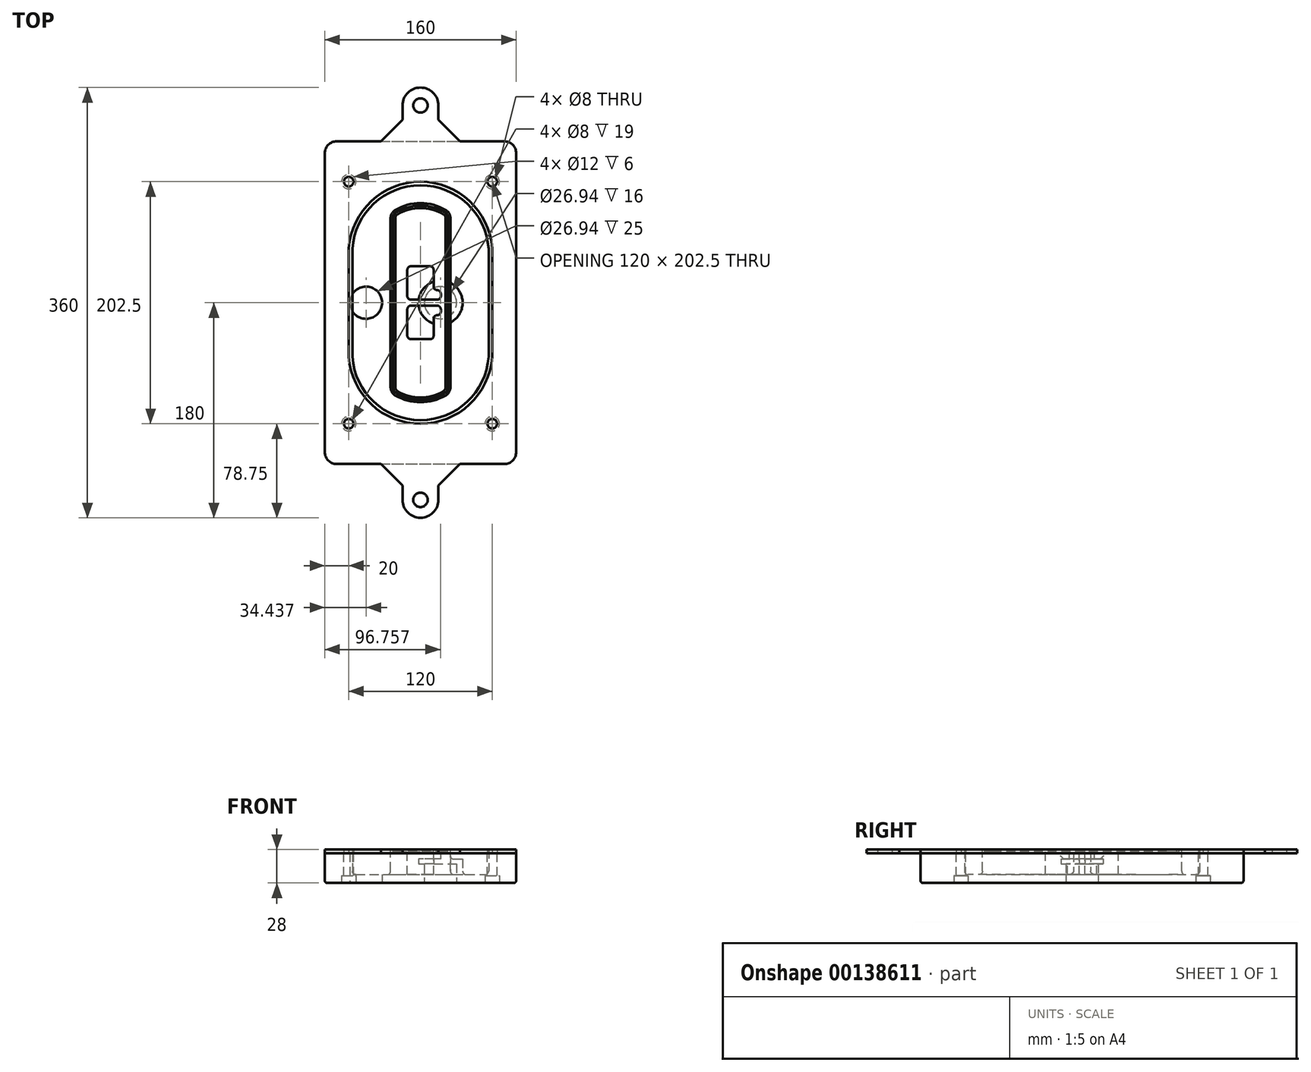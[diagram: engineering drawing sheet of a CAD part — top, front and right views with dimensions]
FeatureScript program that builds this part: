
annotation { "Feature Type Name" : "Feature", "Feature Type Description" : "" }
export const myFeature = defineFeature(function(context is Context, id is Id, definition is map)
    precondition{}
    {
        {
            var Q0;
            Q0=qCreatedBy(makeId("Top.planeOp"),FACE);
            var sketch = newSketch(context, id + "F0", { "sketchPlane" : qUnion([Q0])});
            skPoint(sketch, "E0.rect.middle", {"position": v(0, 0) * mm});
            skLineSegment(sketch, "E1.bottom", {"start": v(-70, -135) * mm, "end": v(70, -135) * mm});
            skLineSegment(sketch, "E1.top", {"start": v(-70, 135) * mm, "end": v(70, 135) * mm});
            skLineSegment(sketch, "E1.left", {"start": v(-80, -125) * mm, "end": v(-80, 125) * mm});
            skLineSegment(sketch, "E1.right", {"start": v(80, -125) * mm, "end": v(80, 125) * mm});
            skLineSegment(sketch, "E2", {"start": v(-80, 135) * mm, "end": v(80, -135) * mm, "construction": true});
            skLineSegment(sketch, "E3", {"start": v(80, 135) * mm, "end": v(-80, -135) * mm, "construction": true});
            skCircle(sketch, "E4", {"center": v(-60, 101.25) * mm, "radius": 4 * mm});
            skCircle(sketch, "E5", {"center": v(60, 101.25) * mm, "radius": 4 * mm});
            skCircle(sketch, "E6", {"center": v(60, -101.25) * mm, "radius": 4 * mm});
            skCircle(sketch, "E7", {"center": v(-60, -101.25) * mm, "radius": 4 * mm});
            skLineSegment(sketch, "E8", {"start": v(-60, 101.25) * mm, "end": v(60, 101.25) * mm, "construction": true});
            skLineSegment(sketch, "E9", {"start": v(60, 101.25) * mm, "end": v(60, -101.25) * mm, "construction": true});
            skLineSegment(sketch, "E10", {"start": v(60, -101.25) * mm, "end": v(-60, -101.25) * mm, "construction": true});
            skLineSegment(sketch, "E11", {"start": v(-60, -101.25) * mm, "end": v(-60, 101.25) * mm, "construction": true});
            skLineSegment(sketch, "E12", {"start": v(-60, 44.66) * mm, "end": v(-60, -44.66) * mm});
            skLineSegment(sketch, "E13", {"start": v(60, 44.66) * mm, "end": v(60, -44.66) * mm});
            skArc(sketch, "E14", {"start": v(59.98, 45.37) * mm, "mid": v(0, 101.25) * mm, "end": v(-59.98, 45.37) * mm});
            skArc(sketch, "E15", {"start": v(-59.98, -45.37) * mm, "mid": v(0, -101.25) * mm, "end": v(59.98, -45.37) * mm});
            skLineSegment(sketch, "E16", {"start": v(-60, 0) * mm, "end": v(60, 0) * mm, "construction": true});
            skPoint(sketch, "E17.visualSharp", {"position": v(-60, -45) * mm});
            skArc(sketch, "E17.filletArc", {"start": v(-60, -44.66) * mm, "mid": v(-60, -45.02) * mm, "end": v(-59.98, -45.37) * mm});
            skPoint(sketch, "E18.visualSharp", {"position": v(-60, 45) * mm});
            skArc(sketch, "E18.filletArc", {"start": v(-59.98, 45.37) * mm, "mid": v(-60, 45.02) * mm, "end": v(-60, 44.66) * mm});
            skPoint(sketch, "E19.visualSharp", {"position": v(60, 45) * mm});
            skArc(sketch, "E19.filletArc", {"start": v(60, 44.66) * mm, "mid": v(60, 45.02) * mm, "end": v(59.98, 45.37) * mm});
            skPoint(sketch, "E20.visualSharp", {"position": v(60, -45) * mm});
            skArc(sketch, "E20.filletArc", {"start": v(59.98, -45.37) * mm, "mid": v(60, -45.02) * mm, "end": v(60, -44.66) * mm});
            skPoint(sketch, "E21.visualSharp", {"position": v(-80, 135) * mm});
            skArc(sketch, "E21.filletArc", {"start": v(-70, 135) * mm, "mid": v(-77.07, 132.07) * mm, "end": v(-80, 125) * mm});
            skPoint(sketch, "E22.visualSharp", {"position": v(80, 135) * mm});
            skArc(sketch, "E22.filletArc", {"start": v(80, 125) * mm, "mid": v(77.07, 132.07) * mm, "end": v(70, 135) * mm});
            skPoint(sketch, "E23.visualSharp", {"position": v(80, -135) * mm});
            skArc(sketch, "E23.filletArc", {"start": v(70, -135) * mm, "mid": v(77.07, -132.07) * mm, "end": v(80, -125) * mm});
            skPoint(sketch, "E24.visualSharp", {"position": v(-80, -135) * mm});
            skArc(sketch, "E24.filletArc", {"start": v(-80, -125) * mm, "mid": v(-77.07, -132.07) * mm, "end": v(-70, -135) * mm});
            skArc(sketch, "E25.0", {"start": v(57, 44.66) * mm, "mid": v(57, 44.9) * mm, "end": v(56.98, 45.16) * mm});
            skLineSegment(sketch, "E25.1", {"start": v(57, 44.66) * mm, "end": v(57, -44.66) * mm});
            skArc(sketch, "E25.2", {"start": v(56.98, -45.16) * mm, "mid": v(57, -44.9) * mm, "end": v(57, -44.66) * mm});
            skArc(sketch, "E25.3", {"start": v(-56.98, -45.16) * mm, "mid": v(0, -98.25) * mm, "end": v(56.98, -45.16) * mm});
            skArc(sketch, "E25.4", {"start": v(-57, -44.66) * mm, "mid": v(-57, -44.9) * mm, "end": v(-56.98, -45.16) * mm});
            skArc(sketch, "E25.5", {"start": v(56.98, 45.16) * mm, "mid": v(0, 98.25) * mm, "end": v(-56.98, 45.16) * mm});
            skLineSegment(sketch, "E25.6", {"start": v(-57, 44.66) * mm, "end": v(-57, -44.66) * mm});
            skArc(sketch, "E25.7", {"start": v(-56.98, 45.16) * mm, "mid": v(-57, 44.9) * mm, "end": v(-57, 44.66) * mm});
            skArc(sketch, "E26.0", {"start": v(-63.97, 45.65) * mm, "mid": v(-64, 45.16) * mm, "end": v(-64, 44.66) * mm});
            skArc(sketch, "E26.1", {"start": v(63.97, 45.65) * mm, "mid": v(0, 105.25) * mm, "end": v(-63.97, 45.65) * mm});
            skArc(sketch, "E26.2", {"start": v(64, 44.66) * mm, "mid": v(64, 45.16) * mm, "end": v(63.97, 45.65) * mm});
            skLineSegment(sketch, "E26.3", {"start": v(64, 44.66) * mm, "end": v(64, -44.66) * mm});
            skArc(sketch, "E26.4", {"start": v(63.97, -45.65) * mm, "mid": v(64, -45.16) * mm, "end": v(64, -44.66) * mm});
            skLineSegment(sketch, "E26.5", {"start": v(-64, 44.66) * mm, "end": v(-64, -44.66) * mm});
            skArc(sketch, "E26.6", {"start": v(-63.97, -45.65) * mm, "mid": v(0, -105.25) * mm, "end": v(63.97, -45.65) * mm});
            skArc(sketch, "E26.7", {"start": v(-64, -44.66) * mm, "mid": v(-64, -45.16) * mm, "end": v(-63.97, -45.65) * mm});
            skSolve(sketch);
        }
        {
            var Q0;
            Q0=makeQuery(id+"F0.imprint","IMPRINT",FACE,{"disambiguationData":[TD([[makeQuery(id+"F0.imprint","IMPRINT",EDGE,{"derivedFrom":sQuery(id+"F0.wireOp",EDGE,"E1.bottom")}),1.0]])]});
            var Q1;
            Q1=makeQuery(id+"F0.imprint","IMPRINT",FACE,{"disambiguationData":[TD([[makeQuery(id+"F0.imprint","IMPRINT",EDGE,{"derivedFrom":sQuery(id+"F0.wireOp",EDGE,"E12")}),1.0]])]});
            var Q2;
            Q2=makeQuery(id+"F0.imprint","IMPRINT",FACE,{"disambiguationData":[TD([[makeQuery(id+"F0.imprint","IMPRINT",EDGE,{"derivedFrom":sQuery(id+"F0.wireOp",EDGE,"E25.0")}),1.0]])]});
            var Q3;
            Q3=makeQuery(id+"F0.imprint","IMPRINT",FACE,{"disambiguationData":[TD([[makeQuery(id+"F0.imprint","IMPRINT",EDGE,{"derivedFrom":sQuery(id+"F0.wireOp",EDGE,"E12")}),-1.0]])]});
            extrude(context, id + "F1", {"entities" : qUnion([Q0, Q1, Q2, Q3]), "oppositeDirection" : true, "depth" : 25 * mm});
        }
        {
            var Q0;
            Q0=makeQuery(id+"F0.imprint","IMPRINT",FACE,{"disambiguationData":[TD([[makeQuery(id+"F0.imprint","IMPRINT",EDGE,{"derivedFrom":sQuery(id+"F0.wireOp",EDGE,"E12")}),1.0]])]});
            extrude(context, id + "F2", {"entities" : qUnion([Q0]), "operationType" : NewBodyOperationType.ADD, "depth" : 3 * mm});
        }
        {
            var Q0;
            Q0=makeQuery(id+"F0.imprint","IMPRINT",FACE,{"disambiguationData":[TD([[makeQuery(id+"F0.imprint","IMPRINT",EDGE,{"derivedFrom":sQuery(id+"F0.wireOp",EDGE,"E25.0")}),1.0]])]});
            extrude(context, id + "F3", {"entities" : qUnion([Q0]), "operationType" : NewBodyOperationType.REMOVE, "oppositeDirection" : true, "depth" : 18 * mm});
        }
        {
            var Q0;
            Q0=makeQuery(id+"F2.opExtrude","CAP_FACE",FACE,{"disambiguationData":[OSD([sQuery(id+"F0.wireOp",EDGE,"E12"),sQuery(id+"F0.wireOp",EDGE,"E13"),sQuery(id+"F0.wireOp",EDGE,"E14"),sQuery(id+"F0.wireOp",EDGE,"E15"),sQuery(id+"F0.wireOp",EDGE,"E17.filletArc"),sQuery(id+"F0.wireOp",EDGE,"E18.filletArc"),sQuery(id+"F0.wireOp",EDGE,"E19.filletArc"),sQuery(id+"F0.wireOp",EDGE,"E20.filletArc"),sQuery(id+"F0.wireOp",EDGE,"E25.0"),sQuery(id+"F0.wireOp",EDGE,"E25.1"),sQuery(id+"F0.wireOp",EDGE,"E25.2"),sQuery(id+"F0.wireOp",EDGE,"E25.3"),sQuery(id+"F0.wireOp",EDGE,"E25.4"),sQuery(id+"F0.wireOp",EDGE,"E25.5"),sQuery(id+"F0.wireOp",EDGE,"E25.6"),sQuery(id+"F0.wireOp",EDGE,"E25.7")])],"isStart":false});
            var sketch = newSketch(context, id + "F4", { "sketchPlane" : qUnion([Q0])});
            skArc(sketch, "E27.0", {"start": v(-20.99, -77.65) * mm, "mid": v(0, -83.25) * mm, "end": v(20.99, -77.65) * mm});
            skArc(sketch, "E28.0", {"start": v(20.99, 77.65) * mm, "mid": v(0, 83.25) * mm, "end": v(-20.99, 77.65) * mm});
            skLineSegment(sketch, "E29", {"start": v(-25, 70.71) * mm, "end": v(-25, -70.71) * mm});
            skLineSegment(sketch, "E30", {"start": v(25, 70.71) * mm, "end": v(25, -70.71) * mm});
            skLineSegment(sketch, "E31", {"start": v(-25, 75.03) * mm, "end": v(25, 75.03) * mm, "construction": true});
            skLineSegment(sketch, "E32", {"start": v(-25, -75.03) * mm, "end": v(25, -75.03) * mm, "construction": true});
            skPoint(sketch, "E33.visualSharp", {"position": v(-25, 75.03) * mm});
            skArc(sketch, "E33.filletArc", {"start": v(-20.99, 77.65) * mm, "mid": v(-23.92, 74.72) * mm, "end": v(-25, 70.71) * mm});
            skPoint(sketch, "E34.visualSharp", {"position": v(25, 75.03) * mm});
            skArc(sketch, "E34.filletArc", {"start": v(25, 70.71) * mm, "mid": v(23.92, 74.72) * mm, "end": v(20.99, 77.65) * mm});
            skPoint(sketch, "E35.visualSharp", {"position": v(25, -75.03) * mm});
            skArc(sketch, "E35.filletArc", {"start": v(20.99, -77.65) * mm, "mid": v(23.92, -74.72) * mm, "end": v(25, -70.71) * mm});
            skPoint(sketch, "E36.visualSharp", {"position": v(-25, -75.03) * mm});
            skArc(sketch, "E36.filletArc", {"start": v(-25, -70.71) * mm, "mid": v(-23.92, -74.72) * mm, "end": v(-20.99, -77.65) * mm});
            skArc(sketch, "E37.0", {"start": v(56.98, 45.16) * mm, "mid": v(0, 98.25) * mm, "end": v(-56.98, 45.16) * mm});
            skArc(sketch, "E37.1", {"start": v(-56.98, 45.16) * mm, "mid": v(-57, 44.9) * mm, "end": v(-57, 44.66) * mm});
            skLineSegment(sketch, "E37.2", {"start": v(-57, 44.66) * mm, "end": v(-57, -44.66) * mm});
            skArc(sketch, "E37.3", {"start": v(-57, -44.66) * mm, "mid": v(-57, -44.9) * mm, "end": v(-56.98, -45.16) * mm});
            skArc(sketch, "E37.4", {"start": v(-56.98, -45.16) * mm, "mid": v(0, -98.25) * mm, "end": v(56.98, -45.16) * mm});
            skArc(sketch, "E37.5", {"start": v(56.98, -45.16) * mm, "mid": v(57, -44.9) * mm, "end": v(57, -44.66) * mm});
            skLineSegment(sketch, "E37.6", {"start": v(57, 44.66) * mm, "end": v(57, -44.66) * mm});
            skArc(sketch, "E37.7", {"start": v(57, 44.66) * mm, "mid": v(57, 44.9) * mm, "end": v(56.98, 45.16) * mm});
            skLineSegment(sketch, "E38.0", {"start": v(23, 70.71) * mm, "end": v(23, -70.71) * mm});
            skArc(sketch, "E38.1", {"start": v(19.99, -75.92) * mm, "mid": v(22.2, -73.72) * mm, "end": v(23, -70.71) * mm});
            skArc(sketch, "E38.2", {"start": v(-19.99, -75.92) * mm, "mid": v(0, -81.25) * mm, "end": v(19.99, -75.92) * mm});
            skArc(sketch, "E38.3", {"start": v(-23, -70.71) * mm, "mid": v(-22.2, -73.72) * mm, "end": v(-19.99, -75.92) * mm});
            skLineSegment(sketch, "E38.4", {"start": v(-23, 70.71) * mm, "end": v(-23, -70.71) * mm});
            skArc(sketch, "E38.5", {"start": v(23, 70.71) * mm, "mid": v(22.2, 73.72) * mm, "end": v(19.99, 75.92) * mm});
            skArc(sketch, "E38.6", {"start": v(-19.99, 75.92) * mm, "mid": v(-22.2, 73.72) * mm, "end": v(-23, 70.71) * mm});
            skArc(sketch, "E38.7", {"start": v(19.99, 75.92) * mm, "mid": v(0, 81.25) * mm, "end": v(-19.99, 75.92) * mm});
            skArc(sketch, "E39.0", {"start": v(21, 70.71) * mm, "mid": v(20.46, 72.72) * mm, "end": v(19, 74.18) * mm});
            skLineSegment(sketch, "E39.1", {"start": v(21, 70.71) * mm, "end": v(21, -70.71) * mm});
            skArc(sketch, "E39.2", {"start": v(19, -74.18) * mm, "mid": v(20.46, -72.72) * mm, "end": v(21, -70.71) * mm});
            skArc(sketch, "E39.3", {"start": v(-19, -74.18) * mm, "mid": v(0, -79.25) * mm, "end": v(19, -74.18) * mm});
            skArc(sketch, "E39.4", {"start": v(-21, -70.71) * mm, "mid": v(-20.46, -72.72) * mm, "end": v(-19, -74.18) * mm});
            skArc(sketch, "E39.5", {"start": v(19, 74.18) * mm, "mid": v(0, 79.25) * mm, "end": v(-19, 74.18) * mm});
            skLineSegment(sketch, "E39.6", {"start": v(-21, 70.71) * mm, "end": v(-21, -70.71) * mm});
            skArc(sketch, "E39.7", {"start": v(-19, 74.18) * mm, "mid": v(-20.46, 72.72) * mm, "end": v(-21, 70.71) * mm});
            skLineSegment(sketch, "E40", {"start": v(-25, 0) * mm, "end": v(25, 0) * mm, "construction": true});
            skLineSegment(sketch, "E41", {"start": v(-11, 5.5) * mm, "end": v(-11, 27.5) * mm});
            skLineSegment(sketch, "E42", {"start": v(-8, 30.5) * mm, "end": v(8, 30.5) * mm});
            skLineSegment(sketch, "E43", {"start": v(11, 27.5) * mm, "end": v(11, 13.5) * mm});
            skLineSegment(sketch, "E44", {"start": v(14, 10.5) * mm, "end": v(14, 10.5) * mm});
            skLineSegment(sketch, "E45", {"start": v(17, 7.5) * mm, "end": v(17, 5.5) * mm});
            skLineSegment(sketch, "E46", {"start": v(14, 2.5) * mm, "end": v(-8, 2.5) * mm});
            skPoint(sketch, "E47.visualSharp", {"position": v(-11, 30.5) * mm});
            skArc(sketch, "E47.filletArc", {"start": v(-8, 30.5) * mm, "mid": v(-10.12, 29.62) * mm, "end": v(-11, 27.5) * mm});
            skPoint(sketch, "E48.visualSharp", {"position": v(11, 30.5) * mm});
            skArc(sketch, "E48.filletArc", {"start": v(11, 27.5) * mm, "mid": v(10.12, 29.62) * mm, "end": v(8, 30.5) * mm});
            skPoint(sketch, "E49.visualSharp", {"position": v(11, 10.5) * mm});
            skArc(sketch, "E49.filletArc", {"start": v(11, 13.5) * mm, "mid": v(11.88, 11.38) * mm, "end": v(14, 10.5) * mm});
            skPoint(sketch, "E50.visualSharp", {"position": v(17, 10.5) * mm});
            skArc(sketch, "E50.filletArc", {"start": v(17, 7.5) * mm, "mid": v(16.12, 9.62) * mm, "end": v(14, 10.5) * mm});
            skPoint(sketch, "E51.visualSharp", {"position": v(17, 2.5) * mm});
            skArc(sketch, "E51.filletArc", {"start": v(14, 2.5) * mm, "mid": v(16.12, 3.38) * mm, "end": v(17, 5.5) * mm});
            skPoint(sketch, "E52.visualSharp", {"position": v(-11, 2.5) * mm});
            skArc(sketch, "E52.filletArc", {"start": v(-11, 5.5) * mm, "mid": v(-10.12, 3.38) * mm, "end": v(-8, 2.5) * mm});
            skLineSegment(sketch, "E53.0.MirrorCS", {"start": v(14, -2.5) * mm, "end": v(-8, -2.5) * mm});
            skArc(sketch, "E54.0.MirrorCS", {"start": v(-11, -5.5) * mm, "mid": v(-10.12, -3.38) * mm, "end": v(-8, -2.5) * mm});
            skLineSegment(sketch, "E55.0.MirrorCS", {"start": v(-11, -5.5) * mm, "end": v(-11, -27.5) * mm});
            skArc(sketch, "E56.0.MirrorCS", {"start": v(-8, -30.5) * mm, "mid": v(-10.12, -29.62) * mm, "end": v(-11, -27.5) * mm});
            skLineSegment(sketch, "E57.0.MirrorCS", {"start": v(-8, -30.5) * mm, "end": v(8, -30.5) * mm});
            skArc(sketch, "E58.0.MirrorCS", {"start": v(11, -27.5) * mm, "mid": v(10.12, -29.62) * mm, "end": v(8, -30.5) * mm});
            skLineSegment(sketch, "E59.0.MirrorCS", {"start": v(11, -27.5) * mm, "end": v(11, -13.5) * mm});
            skArc(sketch, "E60.0.MirrorCS", {"start": v(11, -13.5) * mm, "mid": v(11.88, -11.38) * mm, "end": v(14, -10.5) * mm});
            skArc(sketch, "E61.0.MirrorCS", {"start": v(17, -7.5) * mm, "mid": v(16.12, -9.62) * mm, "end": v(14, -10.5) * mm});
            skLineSegment(sketch, "E62.0.MirrorCS", {"start": v(17, -7.5) * mm, "end": v(17, -5.5) * mm});
            skArc(sketch, "E63.0.MirrorCS", {"start": v(14, -2.5) * mm, "mid": v(16.12, -3.38) * mm, "end": v(17, -5.5) * mm});
            skSolve(sketch);
        }
        {
            var Q0;
            Q0=makeQuery(id+"F4.imprint","IMPRINT",FACE,{"disambiguationData":[TD([[makeQuery(id+"F4.imprint","IMPRINT",EDGE,{"derivedFrom":sQuery(id+"F4.wireOp",EDGE,"E27.0")}),1.0]])]});
            var Q1;
            Q1=makeQuery(id+"F4.imprint","IMPRINT",FACE,{"disambiguationData":[TD([[makeQuery(id+"F4.imprint","IMPRINT",EDGE,{"derivedFrom":sQuery(id+"F4.wireOp",EDGE,"E38.0")}),-1.0]])]});
            var Q2;
            Q2=makeQuery(id+"F4.imprint","IMPRINT",FACE,{"disambiguationData":[TD([[makeQuery(id+"F4.imprint","IMPRINT",EDGE,{"derivedFrom":sQuery(id+"F4.wireOp",EDGE,"E39.0")}),1.0]])]});
            extrude(context, id + "F5", {"entities" : qUnion([Q0, Q1, Q2]), "operationType" : NewBodyOperationType.ADD, "endBound" : BoundingType.UP_TO_NEXT, "oppositeDirection" : true, "depth" : 25 * mm});
        }
        {
            var Q0;
            Q0=makeQuery(id+"F4.imprint","IMPRINT",FACE,{"disambiguationData":[TD([[makeQuery(id+"F4.imprint","IMPRINT",EDGE,{"derivedFrom":sQuery(id+"F4.wireOp",EDGE,"E38.0")}),-1.0]])]});
            extrude(context, id + "F6", {"entities" : qUnion([Q0]), "operationType" : NewBodyOperationType.REMOVE, "oppositeDirection" : true, "depth" : 2 * mm});
        }
        {
            var Q0;
            Q0=makeQuery(id+"F1.opExtrude","CAP_FACE",FACE,{"disambiguationData":[OSD([sQuery(id+"F0.wireOp",EDGE,"E1.bottom"),sQuery(id+"F0.wireOp",EDGE,"E1.top"),sQuery(id+"F0.wireOp",EDGE,"E1.left"),sQuery(id+"F0.wireOp",EDGE,"E1.right"),sQuery(id+"F0.wireOp",EDGE,"E4"),sQuery(id+"F0.wireOp",EDGE,"E5"),sQuery(id+"F0.wireOp",EDGE,"E6"),sQuery(id+"F0.wireOp",EDGE,"E7"),sQuery(id+"F0.wireOp",EDGE,"E21.filletArc"),sQuery(id+"F0.wireOp",EDGE,"E22.filletArc"),sQuery(id+"F0.wireOp",EDGE,"E23.filletArc"),sQuery(id+"F0.wireOp",EDGE,"E24.filletArc")])],"isStart":false});
            var sketch = newSketch(context, id + "F7", { "sketchPlane" : qUnion([Q0])});
            skCircle(sketch, "E64", {"center": v(16.76, 0) * mm, "radius": 13.47 * mm});
            skCircle(sketch, "E65", {"center": v(-45.56, 0) * mm, "radius": 13.47 * mm});
            skLineSegment(sketch, "E66", {"start": v(80, 0) * mm, "end": v(-80, 0) * mm});
            skCircle(sketch, "E67", {"center": v(16.76, 0) * mm, "radius": 18.47 * mm});
            skCircle(sketch, "E68", {"center": v(60, -101.25) * mm, "radius": 6 * mm});
            skCircle(sketch, "E69", {"center": v(-60, -101.25) * mm, "radius": 6 * mm});
            skCircle(sketch, "E70", {"center": v(-60, 101.25) * mm, "radius": 6 * mm});
            skCircle(sketch, "E71", {"center": v(60, 101.25) * mm, "radius": 6 * mm});
            skSolve(sketch);
        }
        {
            var Q0;
            {var subQ1=sQuery(id+"F7.wireOp",EDGE,"E66");var subQ4=sQuery(id+"F7.wireOp",EDGE,"E64");var subQ6=makeQuery(id+"F7.imprint","INTERSECT",VERTEX,{"disambiguationData":[OD(0.0)],"derivedFrom":[subQ4,subQ1]});Q0=makeQuery(id+"F7.imprint","IMPRINT",FACE,{"disambiguationData":[TD([[makeQuery(id+"F7.imprint","IMPRINT",EDGE,{"disambiguationData":[TD([[subQ6,-1.0]])],"derivedFrom":subQ4}),-1.0]])]});}
            var Q1;
            {var subQ0=sQuery(id+"F7.wireOp",EDGE,"E66");var subQ1=sQuery(id+"F7.wireOp",EDGE,"E64");var subQ3=makeQuery(id+"F7.imprint","INTERSECT",VERTEX,{"disambiguationData":[OD(0.0)],"derivedFrom":[subQ1,subQ0]});Q1=makeQuery(id+"F7.imprint","IMPRINT",FACE,{"disambiguationData":[TD([[makeQuery(id+"F7.imprint","IMPRINT",EDGE,{"disambiguationData":[TD([[subQ3,-1.0]])],"derivedFrom":subQ1}),1.0]])]});}
            var Q2;
            {var subQ0=sQuery(id+"F7.wireOp",EDGE,"E66");var subQ1=sQuery(id+"F7.wireOp",EDGE,"E64");var subQ3=makeQuery(id+"F7.imprint","INTERSECT",VERTEX,{"disambiguationData":[OD(0.0)],"derivedFrom":[subQ1,subQ0]});Q2=makeQuery(id+"F7.imprint","IMPRINT",FACE,{"disambiguationData":[TD([[makeQuery(id+"F7.imprint","IMPRINT",EDGE,{"disambiguationData":[TD([[subQ3,1.0]])],"derivedFrom":subQ1}),1.0]])]});}
            var Q3;
            {var subQ1=sQuery(id+"F7.wireOp",EDGE,"E66");var subQ4=sQuery(id+"F7.wireOp",EDGE,"E64");var subQ6=makeQuery(id+"F7.imprint","INTERSECT",VERTEX,{"disambiguationData":[OD(0.0)],"derivedFrom":[subQ4,subQ1]});Q3=makeQuery(id+"F7.imprint","IMPRINT",FACE,{"disambiguationData":[TD([[makeQuery(id+"F7.imprint","IMPRINT",EDGE,{"disambiguationData":[TD([[subQ6,1.0]])],"derivedFrom":subQ4}),-1.0]])]});}
            extrude(context, id + "F8", {"entities" : qUnion([Q0, Q1, Q2, Q3]), "operationType" : NewBodyOperationType.ADD, "oppositeDirection" : true, "depth" : 20 * mm});
        }
        {
            var Q0;
            {var subQ0=sQuery(id+"F7.wireOp",EDGE,"E66");var subQ1=sQuery(id+"F7.wireOp",EDGE,"E64");var subQ3=makeQuery(id+"F7.imprint","INTERSECT",VERTEX,{"disambiguationData":[OD(0.0)],"derivedFrom":[subQ1,subQ0]});Q0=makeQuery(id+"F7.imprint","IMPRINT",FACE,{"disambiguationData":[TD([[makeQuery(id+"F7.imprint","IMPRINT",EDGE,{"disambiguationData":[TD([[subQ3,-1.0]])],"derivedFrom":subQ1}),1.0]])]});}
            var Q1;
            {var subQ0=sQuery(id+"F7.wireOp",EDGE,"E66");var subQ1=sQuery(id+"F7.wireOp",EDGE,"E64");var subQ3=makeQuery(id+"F7.imprint","INTERSECT",VERTEX,{"disambiguationData":[OD(0.0)],"derivedFrom":[subQ1,subQ0]});Q1=makeQuery(id+"F7.imprint","IMPRINT",FACE,{"disambiguationData":[TD([[makeQuery(id+"F7.imprint","IMPRINT",EDGE,{"disambiguationData":[TD([[subQ3,1.0]])],"derivedFrom":subQ1}),1.0]])]});}
            extrude(context, id + "F9", {"entities" : qUnion([Q0, Q1]), "operationType" : NewBodyOperationType.REMOVE, "oppositeDirection" : true, "depth" : 16 * mm});
        }
        {
            var Q0;
            {var subQ0=sQuery(id+"F7.wireOp",EDGE,"E66");var subQ1=sQuery(id+"F7.wireOp",EDGE,"E65");var subQ3=makeQuery(id+"F7.imprint","INTERSECT",VERTEX,{"disambiguationData":[OD(0.0)],"derivedFrom":[subQ1,subQ0]});Q0=makeQuery(id+"F7.imprint","IMPRINT",FACE,{"disambiguationData":[TD([[makeQuery(id+"F7.imprint","IMPRINT",EDGE,{"disambiguationData":[TD([[subQ3,-1.0]])],"derivedFrom":subQ1}),1.0]])]});}
            var Q1;
            {var subQ0=sQuery(id+"F7.wireOp",EDGE,"E66");var subQ1=sQuery(id+"F7.wireOp",EDGE,"E65");var subQ3=makeQuery(id+"F7.imprint","INTERSECT",VERTEX,{"disambiguationData":[OD(0.0)],"derivedFrom":[subQ1,subQ0]});Q1=makeQuery(id+"F7.imprint","IMPRINT",FACE,{"disambiguationData":[TD([[makeQuery(id+"F7.imprint","IMPRINT",EDGE,{"disambiguationData":[TD([[subQ3,1.0]])],"derivedFrom":subQ1}),1.0]])]});}
            extrude(context, id + "F10", {"entities" : qUnion([Q0, Q1]), "operationType" : NewBodyOperationType.REMOVE, "oppositeDirection" : true, "depth" : 25 * mm});
        }
        {
            var Q0;
            Q0=makeQuery(id+"F7.imprint","IMPRINT",FACE,{"disambiguationData":[TD([[makeQuery(id+"F7.imprint","IMPRINT",EDGE,{"derivedFrom":sQuery(id+"F7.wireOp",EDGE,"E68")}),1.0]])]});
            var Q1;
            Q1=makeQuery(id+"F7.imprint","IMPRINT",FACE,{"disambiguationData":[TD([[makeQuery(id+"F7.imprint","IMPRINT",EDGE,{"derivedFrom":makeQuery(id+"F1.opExtrude","CAP_EDGE",EDGE,{"disambiguationData":[OSD([sQuery(id+"F0.wireOp",EDGE,"E5")])],"isStart":false})}),-1.0]])]});
            var Q2;
            Q2=makeQuery(id+"F7.imprint","IMPRINT",FACE,{"disambiguationData":[TD([[makeQuery(id+"F7.imprint","IMPRINT",EDGE,{"derivedFrom":sQuery(id+"F7.wireOp",EDGE,"E69")}),1.0]])]});
            var Q3;
            Q3=makeQuery(id+"F7.imprint","IMPRINT",FACE,{"disambiguationData":[TD([[makeQuery(id+"F7.imprint","IMPRINT",EDGE,{"derivedFrom":makeQuery(id+"F1.opExtrude","CAP_EDGE",EDGE,{"disambiguationData":[OSD([sQuery(id+"F0.wireOp",EDGE,"E4")])],"isStart":false})}),-1.0]])]});
            var Q4;
            Q4=makeQuery(id+"F7.imprint","IMPRINT",FACE,{"disambiguationData":[TD([[makeQuery(id+"F7.imprint","IMPRINT",EDGE,{"derivedFrom":sQuery(id+"F7.wireOp",EDGE,"E70")}),1.0]])]});
            var Q5;
            Q5=makeQuery(id+"F7.imprint","IMPRINT",FACE,{"disambiguationData":[TD([[makeQuery(id+"F7.imprint","IMPRINT",EDGE,{"derivedFrom":makeQuery(id+"F1.opExtrude","CAP_EDGE",EDGE,{"disambiguationData":[OSD([sQuery(id+"F0.wireOp",EDGE,"E7")])],"isStart":false})}),-1.0]])]});
            var Q6;
            Q6=makeQuery(id+"F7.imprint","IMPRINT",FACE,{"disambiguationData":[TD([[makeQuery(id+"F7.imprint","IMPRINT",EDGE,{"derivedFrom":sQuery(id+"F7.wireOp",EDGE,"E71")}),1.0]])]});
            var Q7;
            Q7=makeQuery(id+"F7.imprint","IMPRINT",FACE,{"disambiguationData":[TD([[makeQuery(id+"F7.imprint","IMPRINT",EDGE,{"derivedFrom":makeQuery(id+"F1.opExtrude","CAP_EDGE",EDGE,{"disambiguationData":[OSD([sQuery(id+"F0.wireOp",EDGE,"E6")])],"isStart":false})}),-1.0]])]});
            extrude(context, id + "F11", {"entities" : qUnion([Q0, Q1, Q2, Q3, Q4, Q5, Q6, Q7]), "operationType" : NewBodyOperationType.REMOVE, "oppositeDirection" : true, "depth" : 6 * mm});
        }
        {
            var Q0;
            Q0=makeQuery(id+"F9.boolean.opBoolean","COPY",FACE,{"derivedFrom":makeQuery(id+"F9.opExtrude","CAP_FACE",FACE,{"disambiguationData":[OSD([sQuery(id+"F7.wireOp",EDGE,"E64")])],"isStart":false})});
            var sketch = newSketch(context, id + "F12", { "sketchPlane" : qUnion([Q0])});
            skArc(sketch, "E72.0", {"start": v(11, 17.55) * mm, "mid": v(2.57, 11.82) * mm, "end": v(-1.54, 2.5) * mm});
            skArc(sketch, "E72.1", {"start": v(-1.54, -2.5) * mm, "mid": v(2.57, -11.82) * mm, "end": v(11, -17.55) * mm});
            skLineSegment(sketch, "E73", {"start": v(-1.54, -2.5) * mm, "end": v(14, -2.5) * mm});
            skLineSegment(sketch, "E74.0", {"start": v(14, 2.5) * mm, "end": v(-1.54, 2.5) * mm});
            skArc(sketch, "E74.1", {"start": v(14, 2.5) * mm, "mid": v(16.12, 3.38) * mm, "end": v(17, 5.5) * mm});
            skLineSegment(sketch, "E74.2", {"start": v(17, 7.5) * mm, "end": v(17, 5.5) * mm});
            skArc(sketch, "E74.3", {"start": v(17, 7.5) * mm, "mid": v(16.12, 9.62) * mm, "end": v(14, 10.5) * mm});
            skArc(sketch, "E74.4", {"start": v(11, 13.5) * mm, "mid": v(11.88, 11.38) * mm, "end": v(14, 10.5) * mm});
            skLineSegment(sketch, "E74.5", {"start": v(11, 17.55) * mm, "end": v(11, 13.5) * mm});
            skLineSegment(sketch, "E74.7", {"start": v(14, -2.5) * mm, "end": v(-1.54, -2.5) * mm});
            skArc(sketch, "E74.8", {"start": v(14, -2.5) * mm, "mid": v(16.12, -3.38) * mm, "end": v(17, -5.5) * mm});
            skLineSegment(sketch, "E74.9", {"start": v(17, -7.5) * mm, "end": v(17, -5.5) * mm});
            skArc(sketch, "E74.10", {"start": v(17, -7.5) * mm, "mid": v(16.12, -9.62) * mm, "end": v(14, -10.5) * mm});
            skArc(sketch, "E74.11", {"start": v(11, -13.5) * mm, "mid": v(11.88, -11.38) * mm, "end": v(14, -10.5) * mm});
            skLineSegment(sketch, "E74.12", {"start": v(11, -17.55) * mm, "end": v(11, -13.5) * mm});
            skPoint(sketch, "E75.orphan", {"position": v(11, -27.5) * mm});
            skPoint(sketch, "E76.orphan", {"position": v(-8, -2.5) * mm});
            skPoint(sketch, "E77.orphan", {"position": v(-8, 2.5) * mm});
            skPoint(sketch, "E78.orphan", {"position": v(11, 27.5) * mm});
            skSolve(sketch);
        }
        {
            var Q0;
            {var subQ7=sQuery(id+"F12.wireOp",EDGE,"E72.0");var subQ14=sQuery(id+"F12.wireOp",EDGE,"E72.1");var subQ16=sQuery(id+"F12.wireOp",EDGE,"E74.1");var subQ18=sQuery(id+"F12.wireOp",EDGE,"E74.8");Q0=qUnion([makeQuery(id+"F12.imprint","IMPRINT",FACE,{"disambiguationData":[TD([[makeQuery(id+"F12.imprint","IMPRINT",EDGE,{"derivedFrom":subQ7}),1.0]])]}),makeQuery(id+"F12.imprint","IMPRINT",FACE,{"disambiguationData":[TD([[makeQuery(id+"F12.imprint","IMPRINT",EDGE,{"derivedFrom":subQ14}),1.0]])]}),makeQuery(id+"F12.imprint","IMPRINT",FACE,{"disambiguationData":[TD([[makeQuery(id+"F12.imprint","IMPRINT",EDGE,{"derivedFrom":subQ16}),1.0]])]}),makeQuery(id+"F12.imprint","IMPRINT",FACE,{"disambiguationData":[TD([[makeQuery(id+"F12.imprint","IMPRINT",EDGE,{"derivedFrom":subQ18}),-1.0]])]})]);}
            var Q1;
            Q1=makeQuery(id+"F5.boolean.opBoolean","SPLIT",FACE,{"disambiguationData":[TD([makeQuery(id+"F5.opExtrude","SWEPT_FACE",FACE,{"disambiguationData":[OSD([sQuery(id+"F4.wireOp",EDGE,"E41")])]})])],"derivedFrom":makeQuery(id+"F3.boolean.opBoolean","COPY",FACE,{"derivedFrom":makeQuery(id+"F3.opExtrude","CAP_FACE",FACE,{"disambiguationData":[OSD([sQuery(id+"F0.wireOp",EDGE,"E25.0"),sQuery(id+"F0.wireOp",EDGE,"E25.1"),sQuery(id+"F0.wireOp",EDGE,"E25.2"),sQuery(id+"F0.wireOp",EDGE,"E25.3"),sQuery(id+"F0.wireOp",EDGE,"E25.4"),sQuery(id+"F0.wireOp",EDGE,"E25.5"),sQuery(id+"F0.wireOp",EDGE,"E25.6"),sQuery(id+"F0.wireOp",EDGE,"E25.7")])],"isStart":false})})});
            extrude(context, id + "F13", {"entities" : qUnion([Q0]), "operationType" : NewBodyOperationType.REMOVE, "endBound" : BoundingType.UP_TO_SURFACE, "endBoundEntityFace" : qUnion([Q1]), "depth" : 25 * mm});
        }
        {
            var Q0;
            Q0=makeQuery(id+"F3.boolean.opBoolean","COPY",EDGE,{"derivedFrom":makeQuery(id+"F3.opExtrude","CAP_EDGE",EDGE,{"disambiguationData":[OSD([sQuery(id+"F0.wireOp",EDGE,"E25.6")])],"isStart":false})});
            var Q1;
            Q1=makeQuery(id+"F8.boolean.opBoolean","INTERSECT",EDGE,{"derivedFrom":[makeQuery(id+"F5.opExtrude","SWEPT_FACE",FACE,{"disambiguationData":[OSD([sQuery(id+"F4.wireOp",EDGE,"E30")])]}),makeQuery(id+"F8.opExtrude","CAP_FACE",FACE,{"disambiguationData":[OSD([sQuery(id+"F7.wireOp",EDGE,"E67")])],"isStart":false})]});
            var Q2;
            Q2=makeQuery(id+"F8.boolean.opBoolean","INTERSECT",EDGE,{"disambiguationData":[OD(1.0)],"derivedFrom":[makeQuery(id+"F5.opExtrude","SWEPT_FACE",FACE,{"disambiguationData":[OSD([sQuery(id+"F4.wireOp",EDGE,"E30")])]}),makeQuery(id+"F8.opExtrude","SWEPT_FACE",FACE,{"disambiguationData":[OSD([sQuery(id+"F7.wireOp",EDGE,"E67")])]})]});
            var Q3;
            {var subQ0=sQuery(id+"F4.wireOp",EDGE,"E30");Q3=makeQuery(id+"F8.boolean.opBoolean","SPLIT",EDGE,{"disambiguationData":[TD([makeQuery(id+"F5.opExtrude","SWEPT_FACE",FACE,{"disambiguationData":[OSD([sQuery(id+"F4.wireOp",EDGE,"E35.filletArc")])]})])],"derivedFrom":makeQuery(id+"F5.opExtrude","CAP_EDGE",EDGE,{"disambiguationData":[OSD([subQ0])],"isStart":false})});}
            var Q4;
            {var subQ0=sQuery(id+"F0.wireOp",EDGE,"E25.7");var subQ1=sQuery(id+"F0.wireOp",EDGE,"E25.1");var subQ2=sQuery(id+"F0.wireOp",EDGE,"E25.6");var subQ3=sQuery(id+"F0.wireOp",EDGE,"E25.5");var subQ4=sQuery(id+"F0.wireOp",EDGE,"E25.4");var subQ5=sQuery(id+"F0.wireOp",EDGE,"E25.0");var subQ6=sQuery(id+"F0.wireOp",EDGE,"E25.2");var subQ7=sQuery(id+"F0.wireOp",EDGE,"E25.3");Q4=makeQuery(id+"F8.boolean.opBoolean","INTERSECT",EDGE,{"derivedFrom":[makeQuery(id+"F5.boolean.opBoolean","SPLIT",FACE,{"disambiguationData":[TD([makeQuery(id+"F2.opExtrude","SWEPT_FACE",FACE,{"disambiguationData":[OSD([subQ5])]})])],"derivedFrom":makeQuery(id+"F3.boolean.opBoolean","COPY",FACE,{"derivedFrom":makeQuery(id+"F3.opExtrude","CAP_FACE",FACE,{"disambiguationData":[OSD([subQ5,subQ1,subQ6,subQ7,subQ4,subQ3,subQ2,subQ0])],"isStart":false})})}),makeQuery(id+"F8.opExtrude","SWEPT_FACE",FACE,{"disambiguationData":[OSD([sQuery(id+"F7.wireOp",EDGE,"E67")])]})]});}
            var Q5;
            Q5=makeQuery(id+"F8.boolean.opBoolean","INTERSECT",EDGE,{"disambiguationData":[OD(0.0)],"derivedFrom":[makeQuery(id+"F5.opExtrude","SWEPT_FACE",FACE,{"disambiguationData":[OSD([sQuery(id+"F4.wireOp",EDGE,"E30")])]}),makeQuery(id+"F8.opExtrude","SWEPT_FACE",FACE,{"disambiguationData":[OSD([sQuery(id+"F7.wireOp",EDGE,"E67")])]})]});
            fillet(context, id + "F14", {"entities" : qUnion([Q0, Q1, Q2, Q3, Q4, Q5]), "radius" : 3 * mm, "tangentPropagation" : true, "allowEdgeOverflow" : false});
        }
        {
            var Q0;
            Q0=makeQuery(id+"F1.opExtrude","CAP_EDGE",EDGE,{"disambiguationData":[OSD([sQuery(id+"F0.wireOp",EDGE,"E1.bottom")])],"isStart":false});
            fillet(context, id + "F15", {"entities" : qUnion([Q0]), "radius" : 2 * mm, "tangentPropagation" : true, "allowEdgeOverflow" : false});
        }
        {
            var Q0;
            {var subQ0=sQuery(id+"F0.wireOp",EDGE,"E22.filletArc");var subQ1=sQuery(id+"F0.wireOp",EDGE,"E7");var subQ2=sQuery(id+"F0.wireOp",EDGE,"E6");var subQ3=sQuery(id+"F0.wireOp",EDGE,"E5");var subQ4=sQuery(id+"F0.wireOp",EDGE,"E4");var subQ5=sQuery(id+"F0.wireOp",EDGE,"E1.bottom");var subQ6=sQuery(id+"F0.wireOp",EDGE,"E21.filletArc");var subQ7=sQuery(id+"F0.wireOp",EDGE,"E1.top");var subQ8=sQuery(id+"F0.wireOp",EDGE,"E1.left");var subQ9=sQuery(id+"F0.wireOp",EDGE,"E1.right");var subQ10=sQuery(id+"F0.wireOp",EDGE,"E23.filletArc");var subQ11=sQuery(id+"F0.wireOp",EDGE,"E24.filletArc");Q0=makeQuery(id+"F2.boolean.opBoolean","SPLIT",FACE,{"disambiguationData":[TD([makeQuery(id+"F1.opExtrude","SWEPT_FACE",FACE,{"disambiguationData":[OSD([subQ5])]})])],"derivedFrom":makeQuery(id+"F1.opExtrude","CAP_FACE",FACE,{"disambiguationData":[OSD([subQ5,subQ7,subQ8,subQ9,subQ4,subQ3,subQ2,subQ1,subQ6,subQ0,subQ10,subQ11])],"isStart":true})});}
            var sketch = newSketch(context, id + "F16", { "sketchPlane" : qUnion([Q0])});
            skArc(sketch, "E79.0", {"start": v(-70, 135) * mm, "mid": v(-77.07, 132.07) * mm, "end": v(-80, 125) * mm});
            skLineSegment(sketch, "E79.1", {"start": v(-80, -125) * mm, "end": v(-80, 125) * mm});
            skArc(sketch, "E79.2", {"start": v(-80, -125) * mm, "mid": v(-77.07, -132.07) * mm, "end": v(-70, -135) * mm});
            skLineSegment(sketch, "E79.3", {"start": v(-70, -135) * mm, "end": v(70, -135) * mm});
            skArc(sketch, "E79.4", {"start": v(70, -135) * mm, "mid": v(77.07, -132.07) * mm, "end": v(80, -125) * mm});
            skLineSegment(sketch, "E79.5", {"start": v(80, -125) * mm, "end": v(80, 125) * mm});
            skArc(sketch, "E79.6", {"start": v(80, 125) * mm, "mid": v(77.07, 132.07) * mm, "end": v(70, 135) * mm});
            skLineSegment(sketch, "E79.7", {"start": v(-70, 135) * mm, "end": v(70, 135) * mm});
            skArc(sketch, "E79.8", {"start": v(59.98, 45.37) * mm, "mid": v(0, 101.25) * mm, "end": v(-59.98, 45.37) * mm});
            skCircle(sketch, "E79.9", {"center": v(-60, 101.25) * mm, "radius": 4 * mm});
            skArc(sketch, "E79.10", {"start": v(-59.98, 45.37) * mm, "mid": v(-60, 45.02) * mm, "end": v(-60, 44.66) * mm});
            skLineSegment(sketch, "E79.11", {"start": v(-60, 44.66) * mm, "end": v(-60, -44.66) * mm});
            skArc(sketch, "E79.12", {"start": v(-60, -44.66) * mm, "mid": v(-60, -45.02) * mm, "end": v(-59.98, -45.37) * mm});
            skCircle(sketch, "E79.13", {"center": v(-60, -101.25) * mm, "radius": 4 * mm});
            skArc(sketch, "E79.14", {"start": v(-59.98, -45.37) * mm, "mid": v(0, -101.25) * mm, "end": v(59.98, -45.37) * mm});
            skCircle(sketch, "E79.15", {"center": v(60, -101.25) * mm, "radius": 4 * mm});
            skArc(sketch, "E79.16", {"start": v(59.98, -45.37) * mm, "mid": v(60, -45.02) * mm, "end": v(60, -44.66) * mm});
            skLineSegment(sketch, "E79.17", {"start": v(60, 44.66) * mm, "end": v(60, -44.66) * mm});
            skCircle(sketch, "E79.18", {"center": v(60, 101.25) * mm, "radius": 4 * mm});
            skArc(sketch, "E79.19", {"start": v(60, 44.66) * mm, "mid": v(60, 45.02) * mm, "end": v(59.98, 45.37) * mm});
            skLineSegment(sketch, "E80", {"start": v(0, -41.13) * mm, "end": v(0, 165) * mm, "construction": true});
            skCircle(sketch, "E81", {"center": v(0, 165) * mm, "radius": 6 * mm});
            skLineSegment(sketch, "E82", {"start": v(-15, 165) * mm, "end": v(-15, 153) * mm});
            skLineSegment(sketch, "E83", {"start": v(-15, 153) * mm, "end": v(-33, 135) * mm});
            skLineSegment(sketch, "E84", {"start": v(15, 165) * mm, "end": v(15, 153) * mm});
            skLineSegment(sketch, "E85", {"start": v(15, 153) * mm, "end": v(33, 135) * mm});
            skArc(sketch, "E86", {"start": v(15, 165) * mm, "mid": v(0, 180) * mm, "end": v(-15, 165) * mm});
            skLineSegment(sketch, "E87", {"start": v(92.67, 0) * mm, "end": v(-87.04, 0) * mm, "construction": true});
            skPoint(sketch, "E87.startSnap0", {"position": v(80, 0) * mm});
            skPoint(sketch, "E87.endSnap0", {"position": v(-80, 0) * mm});
            skArc(sketch, "E88.MirrorCS", {"start": v(-15, 165) * mm, "mid": v(0, 180) * mm, "end": v(15, 165) * mm});
            skLineSegment(sketch, "E89.MirrorCS", {"start": v(15, -153) * mm, "end": v(33, -135) * mm});
            skLineSegment(sketch, "E90.MirrorCS", {"start": v(-15, -153) * mm, "end": v(-33, -135) * mm});
            skLineSegment(sketch, "E91.MirrorCS", {"start": v(-15, -165) * mm, "end": v(-15, -153) * mm});
            skCircle(sketch, "E92.MirrorC", {"center": v(0, -165) * mm, "radius": 6 * mm});
            skLineSegment(sketch, "E93.MirrorCS", {"start": v(15, -165) * mm, "end": v(15, -153) * mm});
            skArc(sketch, "E94.MirrorCS", {"start": v(-15, -165) * mm, "mid": v(0, -180) * mm, "end": v(15, -165) * mm});
            skArc(sketch, "E95.MirrorCS", {"start": v(15, -165) * mm, "mid": v(0, -180) * mm, "end": v(-15, -165) * mm});
            skLineSegment(sketch, "E96.MirrorCS", {"start": v(0, 41.13) * mm, "end": v(0, -165) * mm, "construction": true});
            skSolve(sketch);
        }
        {
            var Q0;
            Q0=qSketchRegion(id+"F16",true);
            var Q1;
            Q1=makeQuery(id+"F2.opExtrude","CAP_FACE",FACE,{"disambiguationData":[OSD([sQuery(id+"F0.wireOp",EDGE,"E12"),sQuery(id+"F0.wireOp",EDGE,"E13"),sQuery(id+"F0.wireOp",EDGE,"E14"),sQuery(id+"F0.wireOp",EDGE,"E15"),sQuery(id+"F0.wireOp",EDGE,"E17.filletArc"),sQuery(id+"F0.wireOp",EDGE,"E18.filletArc"),sQuery(id+"F0.wireOp",EDGE,"E19.filletArc"),sQuery(id+"F0.wireOp",EDGE,"E20.filletArc"),sQuery(id+"F0.wireOp",EDGE,"E25.0"),sQuery(id+"F0.wireOp",EDGE,"E25.1"),sQuery(id+"F0.wireOp",EDGE,"E25.2"),sQuery(id+"F0.wireOp",EDGE,"E25.3"),sQuery(id+"F0.wireOp",EDGE,"E25.4"),sQuery(id+"F0.wireOp",EDGE,"E25.5"),sQuery(id+"F0.wireOp",EDGE,"E25.6"),sQuery(id+"F0.wireOp",EDGE,"E25.7")])],"isStart":false});
            extrude(context, id + "F17", {"entities" : qUnion([Q0]), "endBound" : BoundingType.UP_TO_SURFACE, "endBoundEntityFace" : qUnion([Q1]), "depth" : 25 * mm});
        }
    });
